# Revit family: KM5-Wall Mount
name_source: partatom
category: Lighting Fixtures
revit_build: Autodesk Revit 2014 (Build: 20130308_1515(x64)
units: mm (PartAtom-declared; Revit-internal decimal feet)

## types (1)
- KM51-Wall Mount
    Apparent Load = 50 VA
    Assembly Code = D5020280
    CRI = 70
    Certification = Luminaire shall be listed with UL for outdoor,
wet location use, UL1598, UL 8750 and
Canadian CSA Std. C22.2 no.250.
• ANSI C136.31-2010 4G Vibration tested and
compliant.
• IEC 66262 Mechanical Impact Code IK10
• IDA approved, 3000K and warmer CCTs
only
    Default Elevation = 48 "
    Description = KM5 brings the performance and features of the full size KicK luminaires into a smaller form factor for architectural pole or building mount applications
    Finish = Hubbell-Titanium
    Glass = Hubbell-Glass
    IP Rating = IP55
    Lamp = LED
    Light distribution = IES Type II,III,IV
    Load Classification = Lighting
    Manufacturer = Architectural Area Lighting
    Model = KicK™ Mini Medium-Wall Mount
    Photometric Web Link = https://www.hubbell.com
    Photometrics Web = Web KM5 : KM5-T2-5040
    Power Factor = 1
    Product Documentation Link = https://hubbellcdn.com
    Product Page URL = https://www.hubbell.com
    URL = https://www.hubbell.com
    Voltage = 120 V
    Wattage Comments = 50W
    Watts = 50 W

## geometry (parser evidence)
native form markers: Blend x40, Sweep x5
no freeform markers — native parametric forms only
